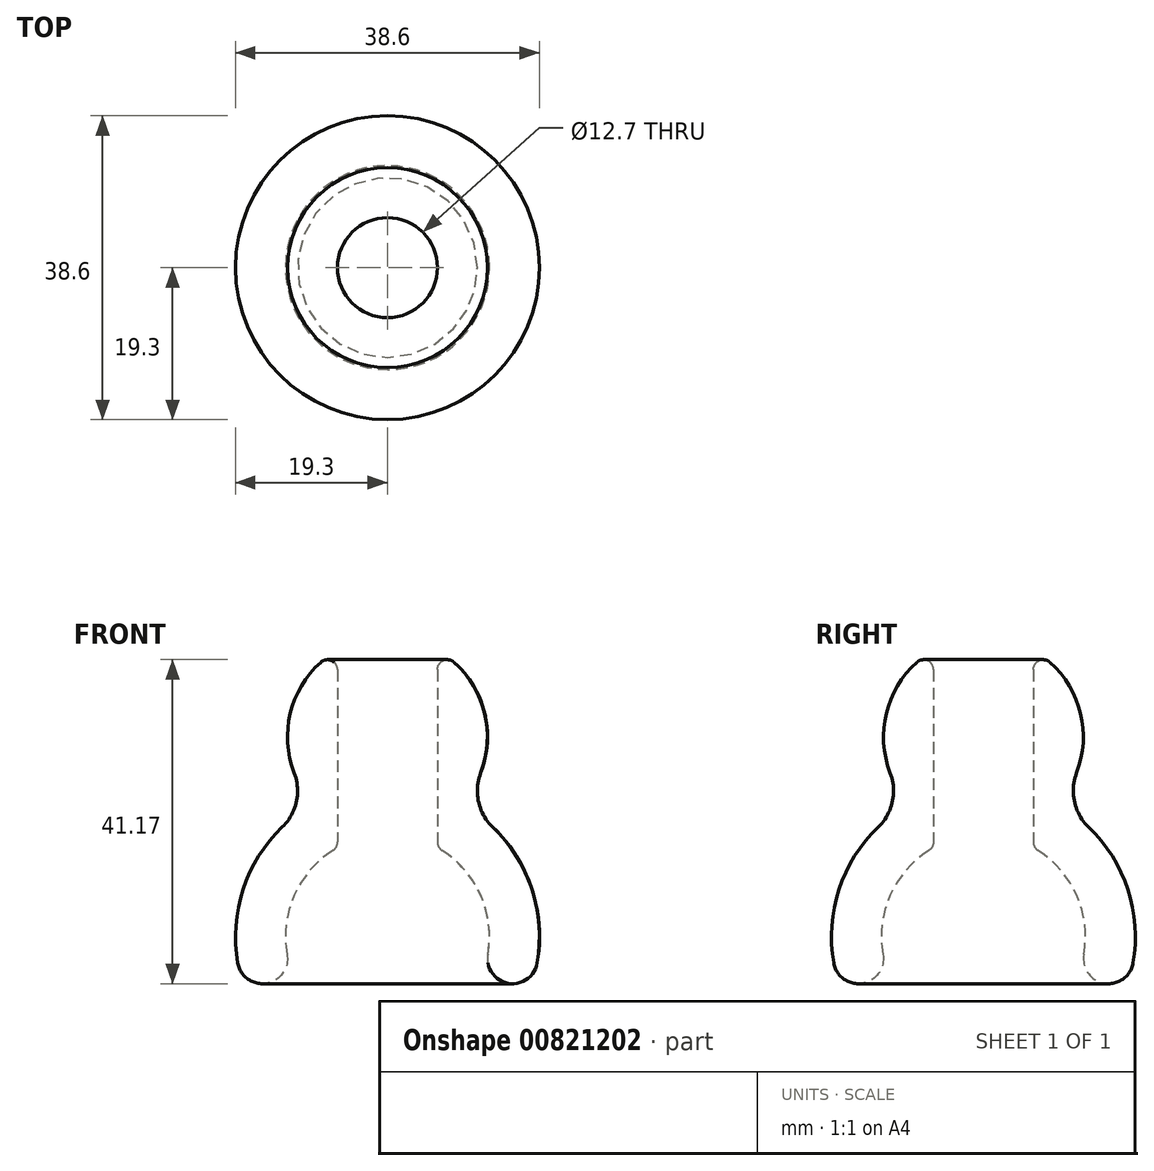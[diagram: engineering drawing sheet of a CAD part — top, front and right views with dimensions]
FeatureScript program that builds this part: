
annotation { "Feature Type Name" : "Feature", "Feature Type Description" : "" }
export const myFeature = defineFeature(function(context is Context, id is Id, definition is map)
    precondition{}
    {
        {
            var Q0;
            Q0=qCreatedBy(makeId("Front.planeOp"),FACE);
            var sketch = newSketch(context, id + "F0", { "sketchPlane" : qUnion([Q0])});
            skLineSegment(sketch, "E0", {"start": v(0, 59.8) * mm, "end": v(0, -59.61) * mm, "construction": true});
            skArc(sketch, "E1", {"start": v(12.76, -2.25) * mm, "mid": v(9.92, 8.33) * mm, "end": v(0, 12.95) * mm});
            skArc(sketch, "E2", {"start": v(0, 12.7) * mm, "mid": v(12.7, 25.4) * mm, "end": v(0, 38.1) * mm});
            skArc(sketch, "E3", {"start": v(19.01, -3.35) * mm, "mid": v(14.79, 12.4) * mm, "end": v(0, 19.3) * mm});
            skLineSegment(sketch, "E4", {"start": v(0, 38.1) * mm, "end": v(0, 12.95) * mm});
            skArc(sketch, "E5", {"start": v(12.76, -2.25) * mm, "mid": v(15.33, -5.93) * mm, "end": v(19.01, -3.35) * mm});
            skArc(sketch, "E6", {"start": v(11.84, 20.8) * mm, "mid": v(11.56, 17.14) * mm, "end": v(13.36, 13.93) * mm});
            skLineSegment(sketch, "E7", {"start": v(0, 0) * mm, "end": v(15.88, -2.8) * mm, "construction": true});
            skSolve(sketch);
        }
        {
            var Q0;
            {var subQ0=sQuery(id+"F0.wireOp",EDGE,"E2");var subQ1=makeQuery(id+"F0.imprint","INTERSECT",VERTEX,{"derivedFrom":[subQ0,sQuery(id+"F0.wireOp",EDGE,"E6")]});Q0=makeQuery(id+"F0.imprint","IMPRINT",FACE,{"disambiguationData":[TD([[makeQuery(id+"F0.imprint","IMPRINT",EDGE,{"disambiguationData":[TD([[subQ1,1.0]])],"derivedFrom":subQ0}),1.0]])]});}
            var Q1;
            {var subQ6=sQuery(id+"F0.wireOp",EDGE,"E5");Q1=makeQuery(id+"F0.imprint","IMPRINT",FACE,{"disambiguationData":[TD([[makeQuery(id+"F0.imprint","IMPRINT",EDGE,{"derivedFrom":subQ6}),1.0]])]});}
            var Q2;
            {var subQ0=sQuery(id+"F0.wireOp",EDGE,"E4");var subQ1=sQuery(id+"F0.wireOp",EDGE,"E1");var subQ2=makeQuery(id+"F0.imprint","INTERSECT",VERTEX,{"derivedFrom":[subQ1,subQ0]});Q2=makeQuery(id+"F0.imprint","IMPRINT",FACE,{"disambiguationData":[TD([[makeQuery(id+"F0.imprint","IMPRINT",EDGE,{"disambiguationData":[TD([[subQ2,1.0]])],"derivedFrom":subQ1}),-1.0]])]});}
            var Q3;
            {var subQ0=sQuery(id+"F0.wireOp",EDGE,"E6");Q3=makeQuery(id+"F0.imprint","IMPRINT",FACE,{"disambiguationData":[TD([[makeQuery(id+"F0.imprint","IMPRINT",EDGE,{"derivedFrom":subQ0}),-1.0]])]});}
            var Q4;
            Q4=sQuery(id+"F0.wireOp",EDGE,"E0");
            revolve(context, id + "F1", {"surfaceOperationType" : NewSurfaceOperationType.NEW, "entities" : qUnion([Q0, Q1, Q2, Q3]), "axis" : qUnion([Q4]), "revolveType" : RevolveType.FULL});
        }
        {
            var Q0;
            Q0=qCreatedBy(makeId("Top.planeOp"),FACE);
            var sketch = newSketch(context, id + "F2", { "sketchPlane" : qUnion([Q0])});
            skCircle(sketch, "E8", {"center": v(0, 0) * mm, "radius": 6.35 * mm});
            skSolve(sketch);
        }
        {
            var Q0;
            Q0=makeQuery(id+"F2.imprint","IMPRINT",FACE,{"disambiguationData":[TD([[makeQuery(id+"F2.imprint","IMPRINT",EDGE,{"derivedFrom":sQuery(id+"F2.wireOp",EDGE,"E8")}),1.0]])]});
            extrude(context, id + "F3", {"entities" : qUnion([Q0]), "operationType" : NewBodyOperationType.REMOVE, "endBound" : BoundingType.THROUGH_ALL, "depth" : 25.4 * mm, "offsetDistance" : 25.4 * mm});
        }
        {
            var Q0;
            Q0=makeQuery(id+"F3.boolean.opBoolean","INTERSECT",EDGE,{"derivedFrom":[makeQuery(id+"F1.opRevolve","SWEPT_FACE",FACE,{"disambiguationData":[OSD([sQuery(id+"F0.wireOp",EDGE,"E2")])]}),makeQuery(id+"F3.opExtrude","SWEPT_FACE",FACE,{"disambiguationData":[OSD([sQuery(id+"F2.wireOp",EDGE,"E8")])]})]});
            var Q1;
            Q1=makeQuery(id+"F3.boolean.opBoolean","INTERSECT",EDGE,{"derivedFrom":[makeQuery(id+"F1.opRevolve","SWEPT_FACE",FACE,{"disambiguationData":[OSD([sQuery(id+"F0.wireOp",EDGE,"E1")])]}),makeQuery(id+"F3.opExtrude","SWEPT_FACE",FACE,{"disambiguationData":[OSD([sQuery(id+"F2.wireOp",EDGE,"E8")])]})]});
            fillet(context, id + "F4", {"entities" : qUnion([Q0, Q1]), "radius" : 1.27 * mm, "tangentPropagation" : true, "allowEdgeOverflow" : false});
        }
    });
